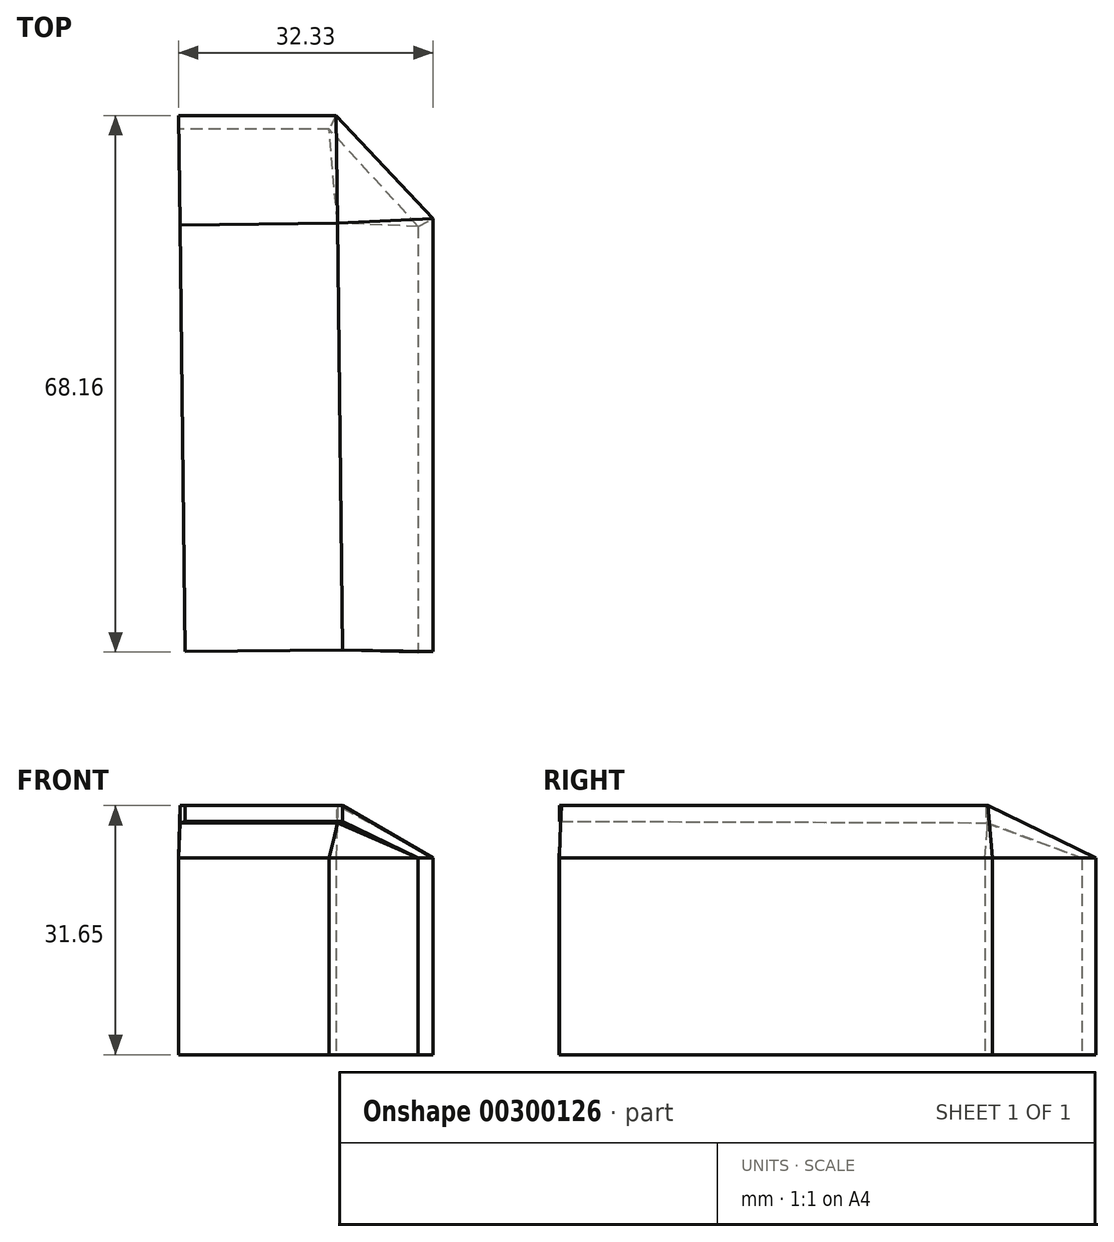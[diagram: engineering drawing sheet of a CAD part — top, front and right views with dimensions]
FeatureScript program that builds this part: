
annotation { "Feature Type Name" : "Feature", "Feature Type Description" : "" }
export const myFeature = defineFeature(function(context is Context, id is Id, definition is map)
    precondition{}
    {
        {
            var Q0;
            Q0=qCreatedBy(makeId("Top.planeOp"),FACE);
            var sketch = newSketch(context, id + "F0", { "sketchPlane" : qUnion([Q0])});
            skLineSegment(sketch, "E0", {"start": v(19.15, 8.64) * mm, "end": v(19.15, -46.36) * mm});
            skLineSegment(sketch, "E1", {"start": v(19.15, 8.64) * mm, "end": v(6.82, 21.75) * mm});
            skLineSegment(sketch, "E2", {"start": v(6.82, 21.75) * mm, "end": v(-13.18, 21.75) * mm});
            skLineSegment(sketch, "E3", {"start": v(17.25, 7.66) * mm, "end": v(17.25, -46.4) * mm});
            skLineSegment(sketch, "E4", {"start": v(17.25, 7.66) * mm, "end": v(5.95, 20) * mm});
            skLineSegment(sketch, "E5", {"start": v(5.95, 20) * mm, "end": v(-13.16, 20) * mm});
            skLineSegment(sketch, "E6", {"start": v(19.15, 8.64) * mm, "end": v(17.25, 7.66) * mm});
            skLineSegment(sketch, "E7", {"start": v(6.82, 21.75) * mm, "end": v(5.95, 20) * mm});
            skLineSegment(sketch, "E8", {"start": v(-13.18, 21.75) * mm, "end": v(-13.16, 20) * mm});
            skLineSegment(sketch, "E9", {"start": v(17.25, -46.4) * mm, "end": v(19.15, -46.36) * mm});
            skSolve(sketch);
        }
        {
            var Q0;
            Q0=makeQuery(id+"F0.imprint","IMPRINT",FACE,{"disambiguationData":[TD([[makeQuery(id+"F0.imprint","IMPRINT",EDGE,{"derivedFrom":sQuery(id+"F0.wireOp",EDGE,"E1")}),1.0]])]});
            var Q1;
            Q1=makeQuery(id+"F0.imprint","IMPRINT",FACE,{"disambiguationData":[TD([[makeQuery(id+"F0.imprint","IMPRINT",EDGE,{"derivedFrom":sQuery(id+"F0.wireOp",EDGE,"E2")}),1.0]])]});
            var Q2;
            Q2=makeQuery(id+"F0.imprint","IMPRINT",FACE,{"disambiguationData":[TD([[makeQuery(id+"F0.imprint","IMPRINT",EDGE,{"derivedFrom":sQuery(id+"F0.wireOp",EDGE,"E0")}),-1.0]])]});
            extrude(context, id + "F1", {"entities" : qUnion([Q0, Q1, Q2]), "depth" : 25 * mm});
        }
        {
            var Q0;
            Q0=makeQuery(id+"F1.opExtrude","SWEPT_FACE",FACE,{"disambiguationData":[OSD([sQuery(id+"F0.wireOp",EDGE,"E8")])]});
            var sketch = newSketch(context, id + "F2", { "sketchPlane" : qUnion([Q0])});
            skLineSegment(sketch, "E10", {"start": v(15.3, 31.65) * mm, "end": v(-7.97, 31.65) * mm});
            skLineSegment(sketch, "E11", {"start": v(15.3, 31.65) * mm, "end": v(46.21, 31.65) * mm});
            skLineSegment(sketch, "E12", {"start": v(-7.97, 31.65) * mm, "end": v(-7.97, 29.46) * mm});
            skLineSegment(sketch, "E13", {"start": v(46.21, 31.65) * mm, "end": v(46.21, 29.65) * mm});
            skLineSegment(sketch, "E14", {"start": v(46.21, 29.65) * mm, "end": v(-7.97, 29.46) * mm});
            skSolve(sketch);
        }
        {
            var Q0;
            Q0 = qSketchRegion(id + "F2", true);
            extrude(context, id + "F3", {"entities" : qUnion([Q0]), "oppositeDirection" : true, "depth" : 20 * mm});
        }
        {
            var Q0;
            Q0=makeQuery(id+"F1.opExtrude","CAP_FACE",FACE,{"disambiguationData":[OSD([sQuery(id+"F0.wireOp",EDGE,"E0"),sQuery(id+"F0.wireOp",EDGE,"E1"),sQuery(id+"F0.wireOp",EDGE,"E2"),sQuery(id+"F0.wireOp",EDGE,"E3"),sQuery(id+"F0.wireOp",EDGE,"E4"),sQuery(id+"F0.wireOp",EDGE,"E5"),sQuery(id+"F0.wireOp",EDGE,"E8"),sQuery(id+"F0.wireOp",EDGE,"E9")])],"isStart":false});
            var sketch = newSketch(context, id + "F4", { "sketchPlane" : qUnion([Q0])});
            skLineSegment(sketch, "E15", {"start": v(17.25, 7.66) * mm, "end": v(19.15, 8.64) * mm});
            skLineSegment(sketch, "E16", {"start": v(19.15, 8.64) * mm, "end": v(6.82, 21.75) * mm});
            skLineSegment(sketch, "E17", {"start": v(6.82, 21.75) * mm, "end": v(5.95, 20) * mm});
            skLineSegment(sketch, "E18", {"start": v(5.95, 20) * mm, "end": v(17.25, 7.66) * mm});
            skLineSegment(sketch, "E19", {"start": v(-13.16, 20) * mm, "end": v(5.95, 20) * mm});
            skLineSegment(sketch, "E20", {"start": v(6.82, 21.75) * mm, "end": v(-13.18, 21.75) * mm});
            skLineSegment(sketch, "E21", {"start": v(-13.18, 21.75) * mm, "end": v(-13.16, 20) * mm});
            skLineSegment(sketch, "E22", {"start": v(19.15, 8.64) * mm, "end": v(19.15, -46.36) * mm});
            skLineSegment(sketch, "E23", {"start": v(19.15, -46.36) * mm, "end": v(17.25, -46.4) * mm});
            skLineSegment(sketch, "E24", {"start": v(17.25, -46.4) * mm, "end": v(17.25, 7.66) * mm});
            skSolve(sketch);
        }
        {
            var Q0;
            Q0=makeQuery(id+"F4.imprint","IMPRINT",FACE,{"disambiguationData":[TD([[makeQuery(id+"F4.imprint","IMPRINT",EDGE,{"derivedFrom":sQuery(id+"F4.wireOp",EDGE,"E15")}),-1.0]])]});
            var Q1;
            Q1=makeQuery(id+"F3.opExtrude","CAP_FACE",FACE,{"disambiguationData":[OSD([sQuery(id+"F2.wireOp",EDGE,"E10"),sQuery(id+"F2.wireOp",EDGE,"E11"),sQuery(id+"F2.wireOp",EDGE,"E12"),sQuery(id+"F2.wireOp",EDGE,"E13"),sQuery(id+"F2.wireOp",EDGE,"E14")])],"isStart":false});
            loft(context, id + "F5", {"sheetProfilesArray" : [{ "sheetProfileEntities" : qUnion([Q0]) }, { "sheetProfileEntities" : qUnion([Q1]) }]});
        }
        {
            var Q0;
            Q0=makeQuery(id+"F3.opExtrude","SWEPT_FACE",FACE,{"disambiguationData":[OSD([sQuery(id+"F2.wireOp",EDGE,"E12")])]});
            var Q1;
            Q1=makeQuery(id+"F4.imprint","IMPRINT",FACE,{"disambiguationData":[TD([[makeQuery(id+"F4.imprint","IMPRINT",EDGE,{"derivedFrom":sQuery(id+"F4.wireOp",EDGE,"E17")}),-1.0]])]});
            loft(context, id + "F6", {"sheetProfilesArray" : [{ "sheetProfileEntities" : qUnion([Q0]) }, { "sheetProfileEntities" : qUnion([Q1]) }]});
        }
        {
            var Q0;
            Q0=makeQuery(id+"F6.opLoft","SWEPT_FACE",FACE,{"disambiguationData":[OSD([sQuery(id+"F2.wireOp",EDGE,"E10"),sQuery(id+"F2.wireOp",EDGE,"E12"),sQuery(id+"F2.wireOp",EDGE,"E14"),sQuery(id+"F4.wireOp",EDGE,"E16"),sQuery(id+"F4.wireOp",EDGE,"E17"),sQuery(id+"F4.wireOp",EDGE,"E18"),sQuery(id+"F4.wireOp",EDGE,"E19"),sQuery(id+"F4.wireOp",EDGE,"E20")])]});
            var Q1;
            Q1=makeQuery(id+"F4.imprint","IMPRINT",FACE,{"disambiguationData":[TD([[makeQuery(id+"F4.imprint","IMPRINT",EDGE,{"derivedFrom":sQuery(id+"F4.wireOp",EDGE,"E15")}),1.0]])]});
            loft(context, id + "F7", {"sheetProfilesArray" : [{ "sheetProfileEntities" : qUnion([Q0]) }, { "sheetProfileEntities" : qUnion([Q1]) }]});
        }
    });
